# Revit family: ASL_Designline_Head & Floor Track
name_source: partatom
category: Detail Items
revit_build: Autodesk Revit 2018 (Build: 20170223_1515(x64)
units: mm (PartAtom-declared; Revit-internal decimal feet)

## family parameters
Rotate with component = No
Section Shape = Not Defined
Shared = Yes

## types (4) — shared parameters
13mm Plasterboard_2 = No
Manufacturer = Aluminate Solutions Limited
Masking Region = Yes
Technical Info = www.aluminate.nz

## per-type parameters (varying)
| type | 13mm Plasterboard | ASL 408 | ASL 415 | ASL 420 | ASL 900 | Masking Region Parametric_1 | Masking Region Parametric_2 | Steel Stud 64mm | Steel Stud 92mm | Type Comments |
| ASL 900 Head & Floor Track 92mm Stud 13mm Gib BS | Yes | No | No | No | Yes | 66 mm  [stored 0.216535 ft] | 66 mm  [stored 0.216535 ft] | No | Yes | ASL Designline ASL 900 Headsection With 92mm Stud 13mm Gib Bothside Wall |
| ASL 415 Head & Floor Track 90x45mm Timber Stud 10mm Gib BS | No | No | Yes | No | No | 61 mm | 61 mm | No | Yes | ASL Designline ASL 415 Headsection With 90x45 Timber Stud 10mm Gib Bothside Wall |
| ASL 408 Head & Floor Track 64mm Stud 2x13mm Gib Ext 13mm Gib Int | No | Yes | No | No | No | 52 mm | 65 mm | Yes | No | ASL Designline ASL 408 Headsection With 64mm Stud 2X13mm Gib Ext 13mm Gib Int Wall |
| ASL 420 Head & Floor Track 92mm Stud 13mm Gib BS | Yes | No | No | Yes | No | 66 mm  [stored 0.216535 ft] | 66 mm  [stored 0.216535 ft] | No | Yes | ASL Designline ASL 420 Headsection With 90mm Stud 13mm Gib Bothside Wall |

note: [stored X ft] marks values corroborated as IEEE doubles in the binary element streams (Revit-internal decimal feet)

## geometry (parser evidence)
native form markers: Sweep x4
no freeform markers — native parametric forms only
